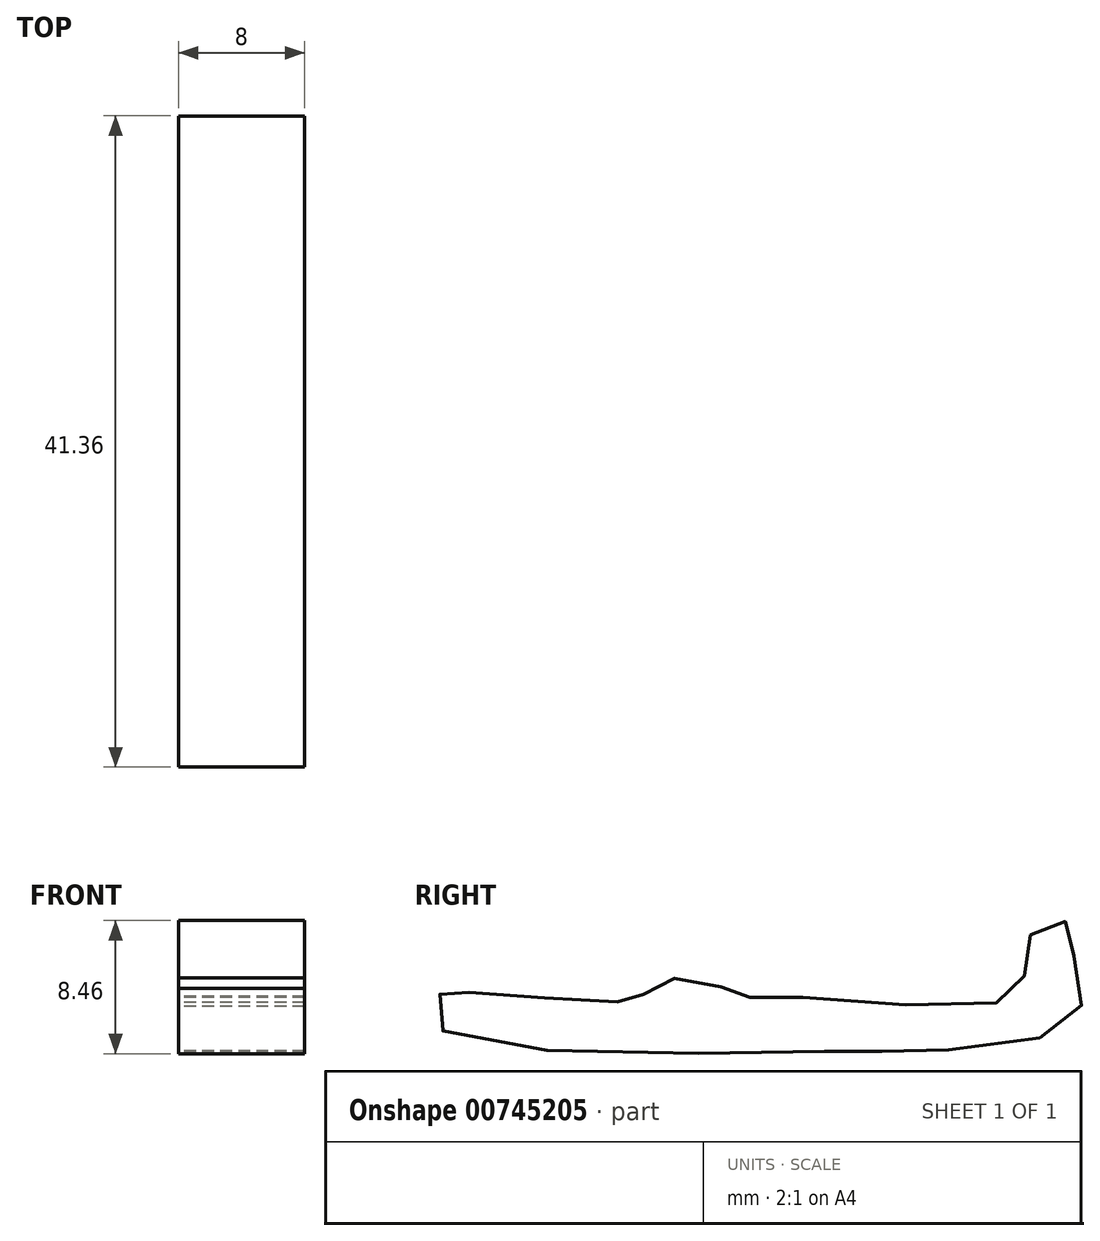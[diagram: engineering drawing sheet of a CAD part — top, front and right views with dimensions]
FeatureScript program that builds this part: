
annotation { "Feature Type Name" : "Feature", "Feature Type Description" : "" }
export const myFeature = defineFeature(function(context is Context, id is Id, definition is map)
    precondition{}
    {
        {
            var Q0;
            Q0=qCreatedBy(makeId("Right.planeOp"),FACE);
            var sketch = newSketch(context, id + "F0", { "sketchPlane" : qUnion([Q0])});
            skFitSpline(sketch, "E0", {"points": [v(0, 0) * mm, v(5.3, 0) * mm, v(15.94, 1.91) * mm, v(15.9, 5.53) * mm, v(15.5, 8.14) * mm, v(13.32, 7.68) * mm, v(12.75, 5) * mm, v(11.23, 3.14) * mm, v(-3.05, 3.5) * mm, v(-5.27, 3.5) * mm, v(-7.28, 4.36) * mm, v(-10.78, 4.34) * mm, v(-11.77, 3.28) * mm, v(-13.49, 3.17) * mm, v(-22.84, 3.8) * mm, v(-24.1, 3.88) * mm, v(-24.81, 1.76) * mm, v(0, 0) * mm]});
            skSolve(sketch);
        }
        {
            var Q0;
            Q0 = qSketchRegion(id + "F0", true);
            extrude(context, id + "F1", {"entities" : qUnion([Q0]), "depth" : 8 * mm, "offsetDistance" : 25 * mm});
        }
    });
